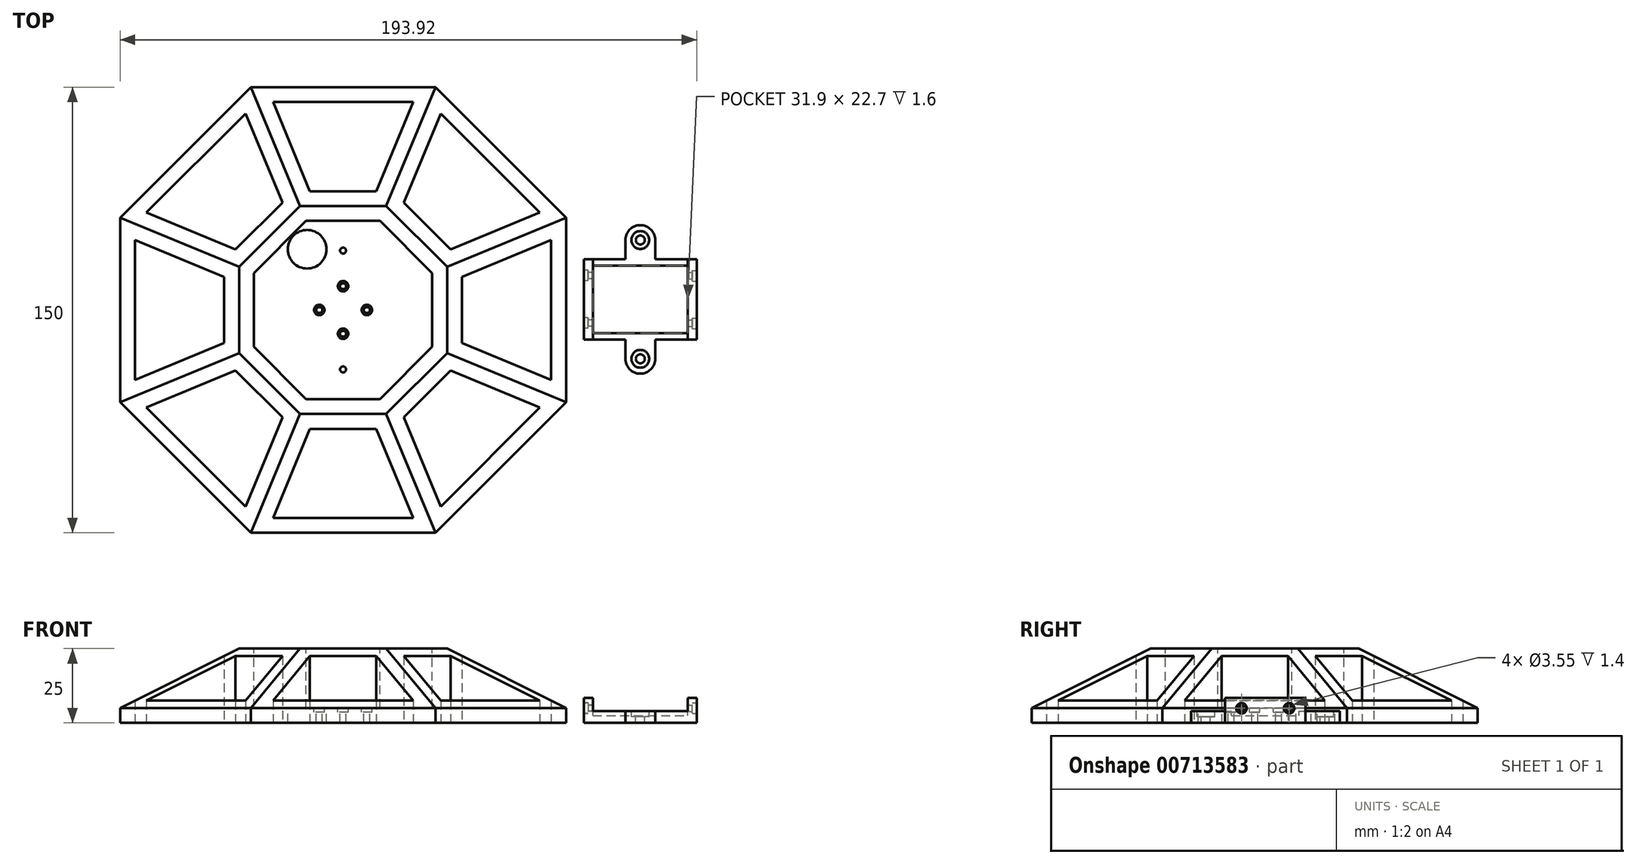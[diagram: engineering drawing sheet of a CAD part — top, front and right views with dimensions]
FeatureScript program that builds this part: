
annotation { "Feature Type Name" : "Feature", "Feature Type Description" : "" }
export const myFeature = defineFeature(function(context is Context, id is Id, definition is map)
    precondition{}
    {
        {
            var Q0;
            Q0=qCreatedBy(makeId("Top.planeOp"),FACE);
            cPlane(context, id + "F0", {"entities" : qUnion([Q0]), "cplaneType" : CPlaneType.OFFSET, "offset" : 0 * mm, "width" : 150 * mm, "height" : 150 * mm});
        }
        {
            var Q0;
            Q0=qCreatedBy(id+"F0.planeOp",FACE);
            var sketch = newSketch(context, id + "F1", { "sketchPlane" : qUnion([Q0])});
            skCircle(sketch, "E0.cCircle", {"center": v(0, 0) * mm, "radius": 75 * mm, "construction": true});
            skLineSegment(sketch, "E0.0", {"start": v(75, 31.07) * mm, "end": v(75, -31.07) * mm});
            skLineSegment(sketch, "E0.1", {"start": v(75, -31.07) * mm, "end": v(31.07, -75) * mm});
            skLineSegment(sketch, "E0.2", {"start": v(31.07, -75) * mm, "end": v(-31.07, -75) * mm});
            skLineSegment(sketch, "E0.3", {"start": v(-31.07, -75) * mm, "end": v(-75, -31.07) * mm});
            skLineSegment(sketch, "E0.4", {"start": v(-75, -31.07) * mm, "end": v(-75, 31.07) * mm});
            skLineSegment(sketch, "E0.5", {"start": v(-75, 31.07) * mm, "end": v(-31.07, 75) * mm});
            skLineSegment(sketch, "E0.6", {"start": v(-31.07, 75) * mm, "end": v(31.07, 75) * mm});
            skLineSegment(sketch, "E0.7", {"start": v(31.07, 75) * mm, "end": v(75, 31.07) * mm});
            skSolve(sketch);
        }
        {
            var Q0;
            Q0=qSketchRegion(id+"F1",true);
            extrude(context, id + "F2", {"entities" : qUnion([Q0]), "depth" : 25 * mm});
        }
        {
            var Q0;
            Q0=makeQuery(id+"F2.opExtrude","CAP_EDGE",EDGE,{"disambiguationData":[OSD([sQuery(id+"F1.wireOp",EDGE,"E0.4")])],"isStart":false});
            var Q1;
            Q1=makeQuery(id+"F2.opExtrude","CAP_EDGE",EDGE,{"disambiguationData":[OSD([sQuery(id+"F1.wireOp",EDGE,"E0.0")])],"isStart":false});
            var Q2;
            Q2=makeQuery(id+"F2.opExtrude","CAP_EDGE",EDGE,{"disambiguationData":[OSD([sQuery(id+"F1.wireOp",EDGE,"E0.7")])],"isStart":false});
            var Q3;
            Q3=makeQuery(id+"F2.opExtrude","CAP_EDGE",EDGE,{"disambiguationData":[OSD([sQuery(id+"F1.wireOp",EDGE,"E0.6")])],"isStart":false});
            var Q4;
            Q4=makeQuery(id+"F2.opExtrude","CAP_EDGE",EDGE,{"disambiguationData":[OSD([sQuery(id+"F1.wireOp",EDGE,"E0.5")])],"isStart":false});
            var Q5;
            Q5=makeQuery(id+"F2.opExtrude","CAP_EDGE",EDGE,{"disambiguationData":[OSD([sQuery(id+"F1.wireOp",EDGE,"E0.3")])],"isStart":false});
            var Q6;
            Q6=makeQuery(id+"F2.opExtrude","CAP_EDGE",EDGE,{"disambiguationData":[OSD([sQuery(id+"F1.wireOp",EDGE,"E0.2")])],"isStart":false});
            var Q7;
            Q7=makeQuery(id+"F2.opExtrude","CAP_EDGE",EDGE,{"disambiguationData":[OSD([sQuery(id+"F1.wireOp",EDGE,"E0.1")])],"isStart":false});
            chamfer(context, id + "F3", {"entities" : qUnion([Q0, Q1, Q2, Q3, Q4, Q5, Q6, Q7]), "chamferType" : ChamferType.TWO_OFFSETS, "width1" : 20 * mm, "oppositeDirection" : false, "width2" : 40 * mm, "tangentPropagation" : true});
        }
        {
            var Q0;
            Q0=makeQuery(id+"F2.opExtrude","CAP_FACE",FACE,{"disambiguationData":[OSD([sQuery(id+"F1.wireOp",EDGE,"E0.0"),sQuery(id+"F1.wireOp",EDGE,"E0.1"),sQuery(id+"F1.wireOp",EDGE,"E0.2"),sQuery(id+"F1.wireOp",EDGE,"E0.3"),sQuery(id+"F1.wireOp",EDGE,"E0.4"),sQuery(id+"F1.wireOp",EDGE,"E0.5"),sQuery(id+"F1.wireOp",EDGE,"E0.6"),sQuery(id+"F1.wireOp",EDGE,"E0.7")])],"isStart":false});
            var sketch = newSketch(context, id + "F4", { "sketchPlane" : qUnion([Q0])});
            skPoint(sketch, "E1.middle", {"position": v(0, 0) * mm});
            skLineSegment(sketch, "E2.0", {"start": v(-14.5, 35) * mm, "end": v(-35, 14.5) * mm});
            skLineSegment(sketch, "E2.1", {"start": v(14.5, 35) * mm, "end": v(-14.5, 35) * mm});
            skLineSegment(sketch, "E2.2", {"start": v(35, 14.5) * mm, "end": v(14.5, 35) * mm});
            skLineSegment(sketch, "E2.3", {"start": v(35, -14.5) * mm, "end": v(35, 14.5) * mm});
            skLineSegment(sketch, "E2.4", {"start": v(14.5, -35) * mm, "end": v(35, -14.5) * mm});
            skLineSegment(sketch, "E2.5", {"start": v(-14.5, -35) * mm, "end": v(14.5, -35) * mm});
            skLineSegment(sketch, "E2.6", {"start": v(-35, -14.5) * mm, "end": v(-14.5, -35) * mm});
            skLineSegment(sketch, "E2.7", {"start": v(-35, 14.5) * mm, "end": v(-35, -14.5) * mm});
            skLineSegment(sketch, "E3.0", {"start": v(-12.43, -30) * mm, "end": v(12.43, -30) * mm});
            skLineSegment(sketch, "E3.1", {"start": v(-30, -12.43) * mm, "end": v(-12.43, -30) * mm});
            skLineSegment(sketch, "E3.2", {"start": v(12.43, -30) * mm, "end": v(30, -12.43) * mm});
            skLineSegment(sketch, "E3.3", {"start": v(-30, 12.43) * mm, "end": v(-30, -12.43) * mm});
            skLineSegment(sketch, "E3.4", {"start": v(30, -12.43) * mm, "end": v(30, 12.43) * mm});
            skLineSegment(sketch, "E3.5", {"start": v(30, 12.43) * mm, "end": v(12.43, 30) * mm});
            skLineSegment(sketch, "E3.6", {"start": v(12.43, 30) * mm, "end": v(-12.43, 30) * mm});
            skLineSegment(sketch, "E3.7", {"start": v(-12.43, 30) * mm, "end": v(-30, 12.43) * mm});
            skSolve(sketch);
        }
        {
            var Q0;
            Q0=makeQuery(id+"F4.imprint","IMPRINT",FACE,{"disambiguationData":[TD([[makeQuery(id+"F4.imprint","IMPRINT",EDGE,{"derivedFrom":sQuery(id+"F4.wireOp",EDGE,"E1.bottom")}),-1.0]])]});
            var Q1;
            Q1=makeQuery(id+"F4.imprint","IMPRINT",FACE,{"disambiguationData":[TD([[makeQuery(id+"F4.imprint","IMPRINT",EDGE,{"derivedFrom":sQuery(id+"F4.wireOp",EDGE,"E3.0")}),1.0]])]});
            extrude(context, id + "F5", {"entities" : qUnion([Q0, Q1]), "operationType" : NewBodyOperationType.REMOVE, "oppositeDirection" : true, "depth" : 20 * mm, "offsetDistance" : 25 * mm});
        }
        {
            var Q0;
            Q0=makeQuery(id+"F5.boolean.opBoolean","COPY",FACE,{"derivedFrom":makeQuery(id+"F5.opExtrude","CAP_FACE",FACE,{"disambiguationData":[OSD([sQuery(id+"F4.wireOp",EDGE,"E3.0"),sQuery(id+"F4.wireOp",EDGE,"E3.1"),sQuery(id+"F4.wireOp",EDGE,"E3.2"),sQuery(id+"F4.wireOp",EDGE,"E3.3"),sQuery(id+"F4.wireOp",EDGE,"E3.4"),sQuery(id+"F4.wireOp",EDGE,"E3.5"),sQuery(id+"F4.wireOp",EDGE,"E3.6"),sQuery(id+"F4.wireOp",EDGE,"E3.7")])],"isStart":false})});
            var sketch = newSketch(context, id + "F6", { "sketchPlane" : qUnion([Q0])});
            skCircle(sketch, "E4", {"center": v(0, 0) * mm, "radius": 8 * mm, "construction": true});
            skCircle(sketch, "E5", {"center": v(0, 8) * mm, "radius": 1 * mm});
            skCircle(sketch, "E6", {"center": v(8, 0) * mm, "radius": 1 * mm});
            skCircle(sketch, "E7", {"center": v(0, -8) * mm, "radius": 1 * mm});
            skCircle(sketch, "E8", {"center": v(-8, 0) * mm, "radius": 1 * mm});
            skCircle(sketch, "E9", {"center": v(0, 0) * mm, "radius": 12 * mm});
            skCircle(sketch, "E10", {"center": v(0, 8) * mm, "radius": 1.75 * mm});
            skCircle(sketch, "E11", {"center": v(8, 0) * mm, "radius": 1.75 * mm});
            skCircle(sketch, "E12", {"center": v(0, -8) * mm, "radius": 1.75 * mm});
            skCircle(sketch, "E13", {"center": v(-8, 0) * mm, "radius": 1.75 * mm});
            skSolve(sketch);
        }
        {
            var Q0;
            Q0=makeQuery(id+"F6.imprint","IMPRINT",FACE,{"disambiguationData":[TD([[makeQuery(id+"F6.imprint","IMPRINT",EDGE,{"derivedFrom":sQuery(id+"F6.wireOp",EDGE,"E6")}),1.0]])]});
            var Q1;
            Q1=makeQuery(id+"F6.imprint","IMPRINT",FACE,{"disambiguationData":[TD([[makeQuery(id+"F6.imprint","IMPRINT",EDGE,{"derivedFrom":sQuery(id+"F6.wireOp",EDGE,"E5")}),1.0]])]});
            var Q2;
            Q2=makeQuery(id+"F6.imprint","IMPRINT",FACE,{"disambiguationData":[TD([[makeQuery(id+"F6.imprint","IMPRINT",EDGE,{"derivedFrom":sQuery(id+"F6.wireOp",EDGE,"E8")}),1.0]])]});
            var Q3;
            Q3=makeQuery(id+"F6.imprint","IMPRINT",FACE,{"disambiguationData":[TD([[makeQuery(id+"F6.imprint","IMPRINT",EDGE,{"derivedFrom":sQuery(id+"F6.wireOp",EDGE,"E7")}),1.0]])]});
            extrude(context, id + "F7", {"entities" : qUnion([Q0, Q1, Q2, Q3]), "operationType" : NewBodyOperationType.REMOVE, "oppositeDirection" : true, "depth" : 25 * mm, "offsetDistance" : 25 * mm});
        }
        {
            var Q0;
            Q0=makeQuery(id+"F2.opExtrude","CAP_FACE",FACE,{"disambiguationData":[OSD([sQuery(id+"F1.wireOp",EDGE,"E0.0"),sQuery(id+"F1.wireOp",EDGE,"E0.1"),sQuery(id+"F1.wireOp",EDGE,"E0.2"),sQuery(id+"F1.wireOp",EDGE,"E0.3"),sQuery(id+"F1.wireOp",EDGE,"E0.4"),sQuery(id+"F1.wireOp",EDGE,"E0.5"),sQuery(id+"F1.wireOp",EDGE,"E0.6"),sQuery(id+"F1.wireOp",EDGE,"E0.7")])],"isStart":true});
            var sketch = newSketch(context, id + "F8", { "sketchPlane" : qUnion([Q0])});
            skLineSegment(sketch, "E14.0", {"start": v(35, -14.5) * mm, "end": v(14.5, -35) * mm});
            skLineSegment(sketch, "E14.1", {"start": v(31.07, -75) * mm, "end": v(14.5, -35) * mm});
            skLineSegment(sketch, "E14.2", {"start": v(31.07, -75) * mm, "end": v(75, -31.07) * mm});
            skLineSegment(sketch, "E14.3", {"start": v(75, -31.07) * mm, "end": v(35, -14.5) * mm});
            skLineSegment(sketch, "E14.4", {"start": v(75, -31.07) * mm, "end": v(75, 31.07) * mm});
            skLineSegment(sketch, "E14.5", {"start": v(75, 31.07) * mm, "end": v(31.07, 75) * mm});
            skLineSegment(sketch, "E14.6", {"start": v(31.07, 75) * mm, "end": v(-31.07, 75) * mm});
            skLineSegment(sketch, "E14.7", {"start": v(-31.07, 75) * mm, "end": v(-75, 31.07) * mm});
            skLineSegment(sketch, "E14.8", {"start": v(-75, 31.07) * mm, "end": v(-75, -31.07) * mm});
            skLineSegment(sketch, "E14.9", {"start": v(-75, -31.07) * mm, "end": v(-31.07, -75) * mm});
            skLineSegment(sketch, "E14.10", {"start": v(-31.07, -75) * mm, "end": v(31.07, -75) * mm});
            skLineSegment(sketch, "E14.11", {"start": v(-31.07, -75) * mm, "end": v(-14.5, -35) * mm});
            skLineSegment(sketch, "E14.12", {"start": v(-35, -14.5) * mm, "end": v(-75, -31.07) * mm});
            skLineSegment(sketch, "E14.13", {"start": v(-35, 14.5) * mm, "end": v(-75, 31.07) * mm});
            skLineSegment(sketch, "E14.14", {"start": v(-14.5, 35) * mm, "end": v(-31.07, 75) * mm});
            skLineSegment(sketch, "E14.15", {"start": v(14.5, 35) * mm, "end": v(31.07, 75) * mm});
            skLineSegment(sketch, "E14.16", {"start": v(75, 31.07) * mm, "end": v(35, 14.5) * mm});
            skLineSegment(sketch, "E14.17", {"start": v(35, 14.5) * mm, "end": v(35, -14.5) * mm});
            skLineSegment(sketch, "E14.18", {"start": v(14.5, 35) * mm, "end": v(35, 14.5) * mm});
            skLineSegment(sketch, "E14.19", {"start": v(-14.5, 35) * mm, "end": v(14.5, 35) * mm});
            skLineSegment(sketch, "E14.20", {"start": v(-35, 14.5) * mm, "end": v(-14.5, 35) * mm});
            skLineSegment(sketch, "E14.21", {"start": v(-35, -14.5) * mm, "end": v(-35, 14.5) * mm});
            skLineSegment(sketch, "E14.22", {"start": v(-14.5, -35) * mm, "end": v(-35, -14.5) * mm});
            skLineSegment(sketch, "E14.23", {"start": v(14.5, -35) * mm, "end": v(-14.5, -35) * mm});
            skLineSegment(sketch, "E15.0", {"start": v(11.16, 40) * mm, "end": v(23.58, 70) * mm});
            skLineSegment(sketch, "E15.1", {"start": v(-11.16, 40) * mm, "end": v(11.16, 40) * mm});
            skLineSegment(sketch, "E15.2", {"start": v(-11.16, 40) * mm, "end": v(-23.58, 70) * mm});
            skLineSegment(sketch, "E15.3", {"start": v(23.58, 70) * mm, "end": v(-23.58, 70) * mm});
            skLineSegment(sketch, "E16.0", {"start": v(20.4, 36.17) * mm, "end": v(32.82, 66.17) * mm});
            skLineSegment(sketch, "E16.1", {"start": v(20.4, 36.17) * mm, "end": v(36.17, 20.4) * mm});
            skLineSegment(sketch, "E16.2", {"start": v(66.17, 32.82) * mm, "end": v(36.17, 20.4) * mm});
            skLineSegment(sketch, "E16.3", {"start": v(66.17, 32.82) * mm, "end": v(32.82, 66.17) * mm});
            skLineSegment(sketch, "E17.0", {"start": v(70, 23.58) * mm, "end": v(40, 11.16) * mm});
            skLineSegment(sketch, "E17.1", {"start": v(70, -23.58) * mm, "end": v(70, 23.58) * mm});
            skLineSegment(sketch, "E17.2", {"start": v(70, -23.58) * mm, "end": v(40, -11.16) * mm});
            skLineSegment(sketch, "E17.3", {"start": v(40, 11.16) * mm, "end": v(40, -11.16) * mm});
            skLineSegment(sketch, "E18.0", {"start": v(66.17, -32.82) * mm, "end": v(36.17, -20.4) * mm});
            skLineSegment(sketch, "E18.1", {"start": v(32.82, -66.17) * mm, "end": v(66.17, -32.82) * mm});
            skLineSegment(sketch, "E18.2", {"start": v(32.82, -66.17) * mm, "end": v(20.4, -36.17) * mm});
            skLineSegment(sketch, "E18.3", {"start": v(36.17, -20.4) * mm, "end": v(20.4, -36.17) * mm});
            skLineSegment(sketch, "E19.0", {"start": v(23.58, -70) * mm, "end": v(11.16, -40) * mm});
            skLineSegment(sketch, "E19.1", {"start": v(-23.58, -70) * mm, "end": v(23.58, -70) * mm});
            skLineSegment(sketch, "E19.2", {"start": v(-23.58, -70) * mm, "end": v(-11.16, -40) * mm});
            skLineSegment(sketch, "E19.3", {"start": v(11.16, -40) * mm, "end": v(-11.16, -40) * mm});
            skLineSegment(sketch, "E20.0", {"start": v(-32.82, -66.17) * mm, "end": v(-20.4, -36.17) * mm});
            skLineSegment(sketch, "E20.1", {"start": v(-66.17, -32.82) * mm, "end": v(-32.82, -66.17) * mm});
            skLineSegment(sketch, "E20.2", {"start": v(-36.17, -20.4) * mm, "end": v(-66.17, -32.82) * mm});
            skLineSegment(sketch, "E20.3", {"start": v(-20.4, -36.17) * mm, "end": v(-36.17, -20.4) * mm});
            skLineSegment(sketch, "E21.0", {"start": v(-40, -11.16) * mm, "end": v(-40, 11.16) * mm});
            skLineSegment(sketch, "E21.1", {"start": v(-40, -11.16) * mm, "end": v(-70, -23.58) * mm});
            skLineSegment(sketch, "E21.2", {"start": v(-70, 23.58) * mm, "end": v(-70, -23.58) * mm});
            skLineSegment(sketch, "E21.3", {"start": v(-40, 11.16) * mm, "end": v(-70, 23.58) * mm});
            skLineSegment(sketch, "E22.0", {"start": v(-36.17, 20.4) * mm, "end": v(-20.4, 36.17) * mm});
            skLineSegment(sketch, "E22.1", {"start": v(-36.17, 20.4) * mm, "end": v(-66.17, 32.82) * mm});
            skLineSegment(sketch, "E22.2", {"start": v(-32.82, 66.17) * mm, "end": v(-66.17, 32.82) * mm});
            skLineSegment(sketch, "E22.3", {"start": v(-20.4, 36.17) * mm, "end": v(-32.82, 66.17) * mm});
            skSolve(sketch);
        }
        {
            var Q0;
            Q0=makeQuery(id+"F8.imprint","IMPRINT",FACE,{"disambiguationData":[TD([[makeQuery(id+"F8.imprint","IMPRINT",EDGE,{"derivedFrom":sQuery(id+"F8.wireOp",EDGE,"E22.0")}),1.0]])]});
            var Q1;
            Q1=makeQuery(id+"F8.imprint","IMPRINT",FACE,{"disambiguationData":[TD([[makeQuery(id+"F8.imprint","IMPRINT",EDGE,{"derivedFrom":sQuery(id+"F8.wireOp",EDGE,"E15.0")}),1.0]])]});
            var Q2;
            Q2=makeQuery(id+"F8.imprint","IMPRINT",FACE,{"disambiguationData":[TD([[makeQuery(id+"F8.imprint","IMPRINT",EDGE,{"derivedFrom":sQuery(id+"F8.wireOp",EDGE,"E16.0")}),-1.0]])]});
            var Q3;
            Q3=makeQuery(id+"F8.imprint","IMPRINT",FACE,{"disambiguationData":[TD([[makeQuery(id+"F8.imprint","IMPRINT",EDGE,{"derivedFrom":sQuery(id+"F8.wireOp",EDGE,"E17.0")}),1.0]])]});
            var Q4;
            Q4=makeQuery(id+"F8.imprint","IMPRINT",FACE,{"disambiguationData":[TD([[makeQuery(id+"F8.imprint","IMPRINT",EDGE,{"derivedFrom":sQuery(id+"F8.wireOp",EDGE,"E18.0")}),1.0]])]});
            var Q5;
            Q5=makeQuery(id+"F8.imprint","IMPRINT",FACE,{"disambiguationData":[TD([[makeQuery(id+"F8.imprint","IMPRINT",EDGE,{"derivedFrom":sQuery(id+"F8.wireOp",EDGE,"E19.0")}),1.0]])]});
            var Q6;
            Q6=makeQuery(id+"F8.imprint","IMPRINT",FACE,{"disambiguationData":[TD([[makeQuery(id+"F8.imprint","IMPRINT",EDGE,{"derivedFrom":sQuery(id+"F8.wireOp",EDGE,"E20.0")}),1.0]])]});
            var Q7;
            Q7=makeQuery(id+"F8.imprint","IMPRINT",FACE,{"disambiguationData":[TD([[makeQuery(id+"F8.imprint","IMPRINT",EDGE,{"derivedFrom":sQuery(id+"F8.wireOp",EDGE,"E21.0")}),1.0]])]});
            extrude(context, id + "F9", {"entities" : qUnion([Q0, Q1, Q2, Q3, Q4, Q5, Q6, Q7]), "operationType" : NewBodyOperationType.REMOVE, "oppositeDirection" : true, "depth" : 25 * mm});
        }
        {
            var Q0;
            Q0=makeQuery(id+"F6.imprint","IMPRINT",FACE,{"disambiguationData":[TD([[makeQuery(id+"F6.imprint","IMPRINT",EDGE,{"derivedFrom":sQuery(id+"F6.wireOp",EDGE,"E8")}),-1.0]])]});
            var Q1;
            Q1=makeQuery(id+"F6.imprint","IMPRINT",FACE,{"disambiguationData":[TD([[makeQuery(id+"F6.imprint","IMPRINT",EDGE,{"derivedFrom":sQuery(id+"F6.wireOp",EDGE,"E5")}),-1.0]])]});
            var Q2;
            Q2=makeQuery(id+"F6.imprint","IMPRINT",FACE,{"disambiguationData":[TD([[makeQuery(id+"F6.imprint","IMPRINT",EDGE,{"derivedFrom":sQuery(id+"F6.wireOp",EDGE,"E6")}),-1.0]])]});
            var Q3;
            Q3=makeQuery(id+"F6.imprint","IMPRINT",FACE,{"disambiguationData":[TD([[makeQuery(id+"F6.imprint","IMPRINT",EDGE,{"derivedFrom":sQuery(id+"F6.wireOp",EDGE,"E7")}),-1.0]])]});
            extrude(context, id + "F10", {"entities" : qUnion([Q0, Q1, Q2, Q3]), "operationType" : NewBodyOperationType.REMOVE, "oppositeDirection" : true, "depth" : 1.4 * mm, "offsetDistance" : 25 * mm});
        }
        {
            var Q0;
            Q0=qCreatedBy(id+"F0.planeOp",FACE);
            var sketch = newSketch(context, id + "F11", { "sketchPlane" : qUnion([Q0])});
            skLineSegment(sketch, "E23", {"start": v(81.02, 17.06) * mm, "end": v(118.92, 17.06) * mm});
            skLineSegment(sketch, "E24", {"start": v(118.92, 17.06) * mm, "end": v(118.92, -9.94) * mm});
            skLineSegment(sketch, "E25", {"start": v(118.92, -9.94) * mm, "end": v(81.02, -9.94) * mm});
            skLineSegment(sketch, "E26", {"start": v(81.02, -9.94) * mm, "end": v(81.02, 17.06) * mm});
            skLineSegment(sketch, "E27", {"start": v(84.02, 17.06) * mm, "end": v(84.02, -9.94) * mm});
            skLineSegment(sketch, "E28", {"start": v(115.92, 17.06) * mm, "end": v(115.92, -9.94) * mm});
            skPoint(sketch, "E29", {"position": v(99.97, 17.06) * mm});
            skArc(sketch, "E30", {"start": v(104.97, 23.56) * mm, "mid": v(99.97, 28.56) * mm, "end": v(94.97, 23.56) * mm});
            skPoint(sketch, "E31", {"position": v(94.97, 17.06) * mm});
            skPoint(sketch, "E32", {"position": v(104.97, 17.06) * mm});
            skLineSegment(sketch, "E33", {"start": v(94.97, 17.06) * mm, "end": v(94.97, 23.56) * mm});
            skLineSegment(sketch, "E34", {"start": v(104.97, 17.06) * mm, "end": v(104.97, 23.56) * mm});
            skPoint(sketch, "E35", {"position": v(99.97, -9.94) * mm});
            skPoint(sketch, "E36", {"position": v(104.97, -9.94) * mm});
            skPoint(sketch, "E37", {"position": v(94.97, -9.94) * mm});
            skArc(sketch, "E38", {"start": v(94.97, -16.44) * mm, "mid": v(99.97, -21.44) * mm, "end": v(104.97, -16.44) * mm});
            skLineSegment(sketch, "E39", {"start": v(94.97, -9.94) * mm, "end": v(94.97, -16.44) * mm});
            skLineSegment(sketch, "E40", {"start": v(104.97, -9.94) * mm, "end": v(104.97, -16.44) * mm});
            skSolve(sketch);
        }
        {
            var Q0;
            Q0=qSketchRegion(id+"F11",true);
            extrude(context, id + "F12", {"entities" : qUnion([Q0]), "depth" : 4 * mm, "offsetDistance" : 25 * mm});
        }
        {
            var Q0;
            {var subQ0=sQuery(id+"F11.wireOp",EDGE,"E26");Q0=makeQuery(id+"F11.imprint","IMPRINT",FACE,{"disambiguationData":[TD([[makeQuery(id+"F11.imprint","IMPRINT",EDGE,{"derivedFrom":subQ0}),-1.0]])]});}
            var Q1;
            {var subQ0=sQuery(id+"F11.wireOp",EDGE,"E24");Q1=makeQuery(id+"F11.imprint","IMPRINT",FACE,{"disambiguationData":[TD([[makeQuery(id+"F11.imprint","IMPRINT",EDGE,{"derivedFrom":subQ0}),-1.0]])]});}
            extrude(context, id + "F13", {"entities" : qUnion([Q0, Q1]), "operationType" : NewBodyOperationType.ADD, "depth" : 8.4 * mm, "offsetDistance" : 25 * mm});
        }
        {
            var Q0;
            Q0=makeQuery(id+"F12.opExtrude","CAP_FACE",FACE,{"disambiguationData":[OSD([sQuery(id+"F11.wireOp",EDGE,"E23"),sQuery(id+"F11.wireOp",EDGE,"E24"),sQuery(id+"F11.wireOp",EDGE,"E25"),sQuery(id+"F11.wireOp",EDGE,"E26"),sQuery(id+"F11.wireOp",EDGE,"E30"),sQuery(id+"F11.wireOp",EDGE,"E33"),sQuery(id+"F11.wireOp",EDGE,"E34"),sQuery(id+"F11.wireOp",EDGE,"E38"),sQuery(id+"F11.wireOp",EDGE,"E39"),sQuery(id+"F11.wireOp",EDGE,"E40")])],"isStart":false});
            var sketch = newSketch(context, id + "F14", { "sketchPlane" : qUnion([Q0])});
            skLineSegment(sketch, "E41.0", {"start": v(81.02, 17.06) * mm, "end": v(118.92, 17.06) * mm});
            skLineSegment(sketch, "E41.1", {"start": v(118.92, -9.94) * mm, "end": v(81.02, -9.94) * mm});
            skLineSegment(sketch, "E42.0", {"start": v(115.92, 17.06) * mm, "end": v(115.92, -9.94) * mm});
            skLineSegment(sketch, "E42.1", {"start": v(84.02, 17.06) * mm, "end": v(84.02, -9.94) * mm});
            skPoint(sketch, "E43", {"position": v(84.02, 3.56) * mm});
            skPoint(sketch, "E44", {"position": v(115.92, 3.56) * mm});
            skLineSegment(sketch, "E45", {"start": v(84.02, 14.91) * mm, "end": v(115.92, 14.91) * mm});
            skLineSegment(sketch, "E46", {"start": v(115.92, -7.79) * mm, "end": v(84.02, -7.79) * mm});
            skSolve(sketch);
        }
        {
            var Q0;
            {var subQ0=sQuery(id+"F14.wireOp",EDGE,"E45");Q0=makeQuery(id+"F14.imprint","IMPRINT",FACE,{"disambiguationData":[TD([[makeQuery(id+"F14.imprint","IMPRINT",EDGE,{"derivedFrom":subQ0}),-1.0]])]});}
            extrude(context, id + "F15", {"entities" : qUnion([Q0]), "operationType" : NewBodyOperationType.REMOVE, "oppositeDirection" : true, "depth" : 1.6 * mm, "offsetDistance" : 25 * mm});
        }
        {
            var Q0;
            {var subQ0=sQuery(id+"F11.wireOp",EDGE,"E24");Q0=makeQuery(id+"F13.boolean.opBoolean","MERGE",FACE,{"derivedFrom":[makeQuery(id+"F12.opExtrude","SWEPT_FACE",FACE,{"disambiguationData":[OSD([subQ0])]}),makeQuery(id+"F13.opExtrude","SWEPT_FACE",FACE,{"disambiguationData":[OSD([subQ0])]})]});}
            var sketch = newSketch(context, id + "F16", { "sketchPlane" : qUnion([Q0])});
            skLineSegment(sketch, "E47.0", {"start": v(-7.79, 2.4) * mm, "end": v(14.91, 2.4) * mm});
            skLineSegment(sketch, "E48", {"start": v(3.56, 2.4) * mm, "end": v(3.56, 4.9) * mm, "construction": true});
            skLineSegment(sketch, "E49", {"start": v(3.56, 4.9) * mm, "end": v(-4.44, 4.9) * mm, "construction": true});
            skLineSegment(sketch, "E50", {"start": v(3.56, 4.9) * mm, "end": v(11.56, 4.9) * mm, "construction": true});
            skCircle(sketch, "E51", {"center": v(11.56, 4.9) * mm, "radius": 1.77 * mm});
            skCircle(sketch, "E52", {"center": v(-4.44, 4.9) * mm, "radius": 1.77 * mm});
            skCircle(sketch, "E53", {"center": v(-4.44, 4.9) * mm, "radius": 1.05 * mm});
            skCircle(sketch, "E54", {"center": v(11.56, 4.9) * mm, "radius": 1.05 * mm});
            skSolve(sketch);
        }
        {
            var Q0;
            Q0=makeQuery(id+"F16.imprint","IMPRINT",FACE,{"disambiguationData":[TD([[makeQuery(id+"F16.imprint","IMPRINT",EDGE,{"derivedFrom":sQuery(id+"F16.wireOp",EDGE,"E54")}),1.0]])]});
            var Q1;
            Q1=makeQuery(id+"F16.imprint","IMPRINT",FACE,{"disambiguationData":[TD([[makeQuery(id+"F16.imprint","IMPRINT",EDGE,{"derivedFrom":sQuery(id+"F16.wireOp",EDGE,"E53")}),1.0]])]});
            extrude(context, id + "F17", {"entities" : qUnion([Q0, Q1]), "operationType" : NewBodyOperationType.REMOVE, "oppositeDirection" : true, "depth" : 5 * mm, "offsetDistance" : 25 * mm});
        }
        {
            var Q0;
            Q0=makeQuery(id+"F16.imprint","IMPRINT",FACE,{"disambiguationData":[TD([[makeQuery(id+"F16.imprint","IMPRINT",EDGE,{"derivedFrom":sQuery(id+"F16.wireOp",EDGE,"E52")}),1.0]])]});
            var Q1;
            Q1=makeQuery(id+"F16.imprint","IMPRINT",FACE,{"disambiguationData":[TD([[makeQuery(id+"F16.imprint","IMPRINT",EDGE,{"derivedFrom":sQuery(id+"F16.wireOp",EDGE,"E51")}),1.0]])]});
            extrude(context, id + "F18", {"entities" : qUnion([Q0, Q1]), "operationType" : NewBodyOperationType.REMOVE, "oppositeDirection" : true, "depth" : 1.4 * mm, "offsetDistance" : 25 * mm});
        }
        {
            var Q0;
            {var subQ0=sQuery(id+"F11.wireOp",EDGE,"E26");Q0=makeQuery(id+"F13.boolean.opBoolean","MERGE",FACE,{"derivedFrom":[makeQuery(id+"F12.opExtrude","SWEPT_FACE",FACE,{"disambiguationData":[OSD([subQ0])]}),makeQuery(id+"F13.opExtrude","SWEPT_FACE",FACE,{"disambiguationData":[OSD([subQ0])]})]});}
            var sketch = newSketch(context, id + "F19", { "sketchPlane" : qUnion([Q0])});
            skLineSegment(sketch, "E55.0", {"start": v(7.79, 2.4) * mm, "end": v(-14.91, 2.4) * mm});
            skLineSegment(sketch, "E56", {"start": v(-3.56, 2.4) * mm, "end": v(-3.58, 4.9) * mm, "construction": true});
            skLineSegment(sketch, "E57", {"start": v(-3.58, 4.9) * mm, "end": v(-11.58, 4.85) * mm, "construction": true});
            skLineSegment(sketch, "E58", {"start": v(-3.58, 4.9) * mm, "end": v(4.42, 4.95) * mm, "construction": true});
            skCircle(sketch, "E59", {"center": v(-11.58, 4.85) * mm, "radius": 1.77 * mm});
            skCircle(sketch, "E60", {"center": v(4.42, 4.95) * mm, "radius": 1.77 * mm});
            skCircle(sketch, "E61", {"center": v(-11.58, 4.85) * mm, "radius": 1.05 * mm});
            skCircle(sketch, "E62", {"center": v(4.42, 4.95) * mm, "radius": 1.05 * mm});
            skSolve(sketch);
        }
        {
            var Q0;
            Q0=makeQuery(id+"F19.imprint","IMPRINT",FACE,{"disambiguationData":[TD([[makeQuery(id+"F19.imprint","IMPRINT",EDGE,{"derivedFrom":sQuery(id+"F19.wireOp",EDGE,"E62")}),1.0]])]});
            var Q1;
            Q1=makeQuery(id+"F19.imprint","IMPRINT",FACE,{"disambiguationData":[TD([[makeQuery(id+"F19.imprint","IMPRINT",EDGE,{"derivedFrom":sQuery(id+"F19.wireOp",EDGE,"E61")}),1.0]])]});
            extrude(context, id + "F20", {"entities" : qUnion([Q0, Q1]), "operationType" : NewBodyOperationType.REMOVE, "oppositeDirection" : true, "depth" : 4 * mm, "offsetDistance" : 25 * mm});
        }
        {
            var Q0;
            Q0=makeQuery(id+"F19.imprint","IMPRINT",FACE,{"disambiguationData":[TD([[makeQuery(id+"F19.imprint","IMPRINT",EDGE,{"derivedFrom":sQuery(id+"F19.wireOp",EDGE,"E59")}),1.0]])]});
            var Q1;
            Q1=makeQuery(id+"F19.imprint","IMPRINT",FACE,{"disambiguationData":[TD([[makeQuery(id+"F19.imprint","IMPRINT",EDGE,{"derivedFrom":sQuery(id+"F19.wireOp",EDGE,"E60")}),1.0]])]});
            extrude(context, id + "F21", {"entities" : qUnion([Q0, Q1]), "operationType" : NewBodyOperationType.REMOVE, "oppositeDirection" : true, "depth" : 1.4 * mm, "offsetDistance" : 25 * mm});
        }
        {
            var Q0;
            {var subQ0=sQuery(id+"F11.wireOp",EDGE,"E24");var subQ1=sQuery(id+"F11.wireOp",EDGE,"E23");var subQ5=sQuery(id+"F11.wireOp",EDGE,"E26");var subQ9=sQuery(id+"F11.wireOp",EDGE,"E33");var subQ10=sQuery(id+"F11.wireOp",EDGE,"E34");var subQ11=sQuery(id+"F11.wireOp",EDGE,"E30");Q0=makeQuery(id+"F15.boolean.opBoolean","SPLIT",FACE,{"disambiguationData":[TD([makeQuery(id+"F12.opExtrude","SWEPT_FACE",FACE,{"disambiguationData":[OSD([subQ11])]})])],"derivedFrom":makeQuery(id+"F12.opExtrude","CAP_FACE",FACE,{"disambiguationData":[OSD([subQ1,subQ0,sQuery(id+"F11.wireOp",EDGE,"E25"),subQ5,subQ11,subQ9,subQ10,sQuery(id+"F11.wireOp",EDGE,"E38"),sQuery(id+"F11.wireOp",EDGE,"E39"),sQuery(id+"F11.wireOp",EDGE,"E40")])],"isStart":false})});}
            var sketch = newSketch(context, id + "F22", { "sketchPlane" : qUnion([Q0])});
            skPoint(sketch, "E63.0", {"position": v(99.97, 23.56) * mm});
            skPoint(sketch, "E63.1", {"position": v(99.97, -16.44) * mm});
            skCircle(sketch, "E64", {"center": v(99.97, -16.44) * mm, "radius": 3 * mm});
            skCircle(sketch, "E65", {"center": v(99.97, 23.56) * mm, "radius": 3 * mm});
            skCircle(sketch, "E66", {"center": v(99.97, 23.56) * mm, "radius": 1.5 * mm});
            skCircle(sketch, "E67", {"center": v(99.97, -16.44) * mm, "radius": 1.5 * mm});
            skSolve(sketch);
        }
        {
            var Q0;
            Q0=makeQuery(id+"F22.imprint","IMPRINT",FACE,{"disambiguationData":[TD([[makeQuery(id+"F22.imprint","IMPRINT",EDGE,{"derivedFrom":sQuery(id+"F22.wireOp",EDGE,"E66")}),1.0]])]});
            var Q1;
            Q1=makeQuery(id+"F22.imprint","IMPRINT",FACE,{"disambiguationData":[TD([[makeQuery(id+"F22.imprint","IMPRINT",EDGE,{"derivedFrom":sQuery(id+"F22.wireOp",EDGE,"E67")}),1.0]])]});
            extrude(context, id + "F23", {"entities" : qUnion([Q0, Q1]), "operationType" : NewBodyOperationType.REMOVE, "oppositeDirection" : true, "depth" : 25 * mm, "offsetDistance" : 25 * mm});
        }
        {
            var Q0;
            Q0=makeQuery(id+"F22.imprint","IMPRINT",FACE,{"disambiguationData":[TD([[makeQuery(id+"F22.imprint","IMPRINT",EDGE,{"derivedFrom":sQuery(id+"F22.wireOp",EDGE,"E64")}),1.0]])]});
            var Q1;
            Q1=makeQuery(id+"F22.imprint","IMPRINT",FACE,{"disambiguationData":[TD([[makeQuery(id+"F22.imprint","IMPRINT",EDGE,{"derivedFrom":sQuery(id+"F22.wireOp",EDGE,"E65")}),1.0]])]});
            extrude(context, id + "F24", {"entities" : qUnion([Q0, Q1]), "operationType" : NewBodyOperationType.REMOVE, "oppositeDirection" : true, "depth" : 2 * mm, "offsetDistance" : 25 * mm});
        }
        {
            var Q0;
            Q0=makeQuery(id+"F5.boolean.opBoolean","COPY",FACE,{"derivedFrom":makeQuery(id+"F5.opExtrude","CAP_FACE",FACE,{"disambiguationData":[OSD([sQuery(id+"F4.wireOp",EDGE,"E3.0"),sQuery(id+"F4.wireOp",EDGE,"E3.1"),sQuery(id+"F4.wireOp",EDGE,"E3.2"),sQuery(id+"F4.wireOp",EDGE,"E3.3"),sQuery(id+"F4.wireOp",EDGE,"E3.4"),sQuery(id+"F4.wireOp",EDGE,"E3.5"),sQuery(id+"F4.wireOp",EDGE,"E3.6"),sQuery(id+"F4.wireOp",EDGE,"E3.7")])],"isStart":false})});
            var sketch = newSketch(context, id + "F25", { "sketchPlane" : qUnion([Q0])});
            skLineSegment(sketch, "E68", {"start": v(0, 0) * mm, "end": v(0, 20) * mm, "construction": true});
            skLineSegment(sketch, "E69", {"start": v(0, 0) * mm, "end": v(0, -20) * mm, "construction": true});
            skCircle(sketch, "E70", {"center": v(0, -20) * mm, "radius": 1 * mm});
            skCircle(sketch, "E71", {"center": v(0, 20) * mm, "radius": 1 * mm});
            skSolve(sketch);
        }
        {
            var Q0;
            Q0=makeQuery(id+"F25.imprint","IMPRINT",FACE,{"disambiguationData":[TD([[makeQuery(id+"F25.imprint","IMPRINT",EDGE,{"derivedFrom":sQuery(id+"F25.wireOp",EDGE,"E71")}),1.0]])]});
            var Q1;
            Q1=makeQuery(id+"F25.imprint","IMPRINT",FACE,{"disambiguationData":[TD([[makeQuery(id+"F25.imprint","IMPRINT",EDGE,{"derivedFrom":sQuery(id+"F25.wireOp",EDGE,"E70")}),1.0]])]});
            extrude(context, id + "F26", {"entities" : qUnion([Q0, Q1]), "operationType" : NewBodyOperationType.REMOVE, "oppositeDirection" : true, "depth" : 25 * mm, "offsetDistance" : 25 * mm});
        }
        {
            var Q0;
            Q0=makeQuery(id+"F5.boolean.opBoolean","COPY",FACE,{"derivedFrom":makeQuery(id+"F5.opExtrude","CAP_FACE",FACE,{"disambiguationData":[OSD([sQuery(id+"F4.wireOp",EDGE,"E3.0"),sQuery(id+"F4.wireOp",EDGE,"E3.1"),sQuery(id+"F4.wireOp",EDGE,"E3.2"),sQuery(id+"F4.wireOp",EDGE,"E3.3"),sQuery(id+"F4.wireOp",EDGE,"E3.4"),sQuery(id+"F4.wireOp",EDGE,"E3.5"),sQuery(id+"F4.wireOp",EDGE,"E3.6"),sQuery(id+"F4.wireOp",EDGE,"E3.7")])],"isStart":false})});
            var sketch = newSketch(context, id + "F27", { "sketchPlane" : qUnion([Q0])});
            skLineSegment(sketch, "E72", {"start": v(-18.95, 13.5) * mm, "end": v(18.95, 13.5) * mm, "construction": true});
            skLineSegment(sketch, "E73", {"start": v(18.95, 13.5) * mm, "end": v(18.95, -13.5) * mm, "construction": true});
            skLineSegment(sketch, "E74", {"start": v(18.95, -13.5) * mm, "end": v(-18.95, -13.5) * mm, "construction": true});
            skLineSegment(sketch, "E75", {"start": v(-18.95, -13.5) * mm, "end": v(-18.95, 13.5) * mm, "construction": true});
            skLineSegment(sketch, "E76", {"start": v(-15.95, 13.5) * mm, "end": v(-15.95, -13.5) * mm, "construction": true});
            skLineSegment(sketch, "E77", {"start": v(15.95, 13.5) * mm, "end": v(15.95, -13.5) * mm, "construction": true});
            skPoint(sketch, "E78", {"position": v(0, 13.5) * mm});
            skArc(sketch, "E79", {"start": v(5, 20) * mm, "mid": v(0, 25) * mm, "end": v(-5, 20) * mm, "construction": true});
            skPoint(sketch, "E80", {"position": v(-5, 13.5) * mm});
            skPoint(sketch, "E81", {"position": v(5, 13.5) * mm});
            skLineSegment(sketch, "E82", {"start": v(-5, 13.5) * mm, "end": v(-5, 20) * mm, "construction": true});
            skLineSegment(sketch, "E83", {"start": v(5, 13.5) * mm, "end": v(5, 20) * mm, "construction": true});
            skPoint(sketch, "E84", {"position": v(0, -13.5) * mm});
            skPoint(sketch, "E85", {"position": v(5, -13.5) * mm});
            skPoint(sketch, "E86", {"position": v(-5, -13.5) * mm});
            skArc(sketch, "E87", {"start": v(-5, -20) * mm, "mid": v(0, -25) * mm, "end": v(5, -20) * mm, "construction": true});
            skLineSegment(sketch, "E88", {"start": v(-5, -13.5) * mm, "end": v(-5, -20) * mm, "construction": true});
            skLineSegment(sketch, "E89", {"start": v(5, -13.5) * mm, "end": v(5, -20) * mm, "construction": true});
            skCircle(sketch, "E90", {"center": v(-12.1, 20.44) * mm, "radius": 6.5 * mm});
            skSolve(sketch);
        }
        {
            var Q0;
            Q0=makeQuery(id+"F27.imprint","IMPRINT",FACE,{"disambiguationData":[TD([[makeQuery(id+"F27.imprint","IMPRINT",EDGE,{"derivedFrom":sQuery(id+"F27.wireOp",EDGE,"E90")}),1.0]])]});
            extrude(context, id + "F28", {"entities" : qUnion([Q0]), "operationType" : NewBodyOperationType.REMOVE, "oppositeDirection" : true, "depth" : 25 * mm, "offsetDistance" : 25 * mm});
        }
    });
